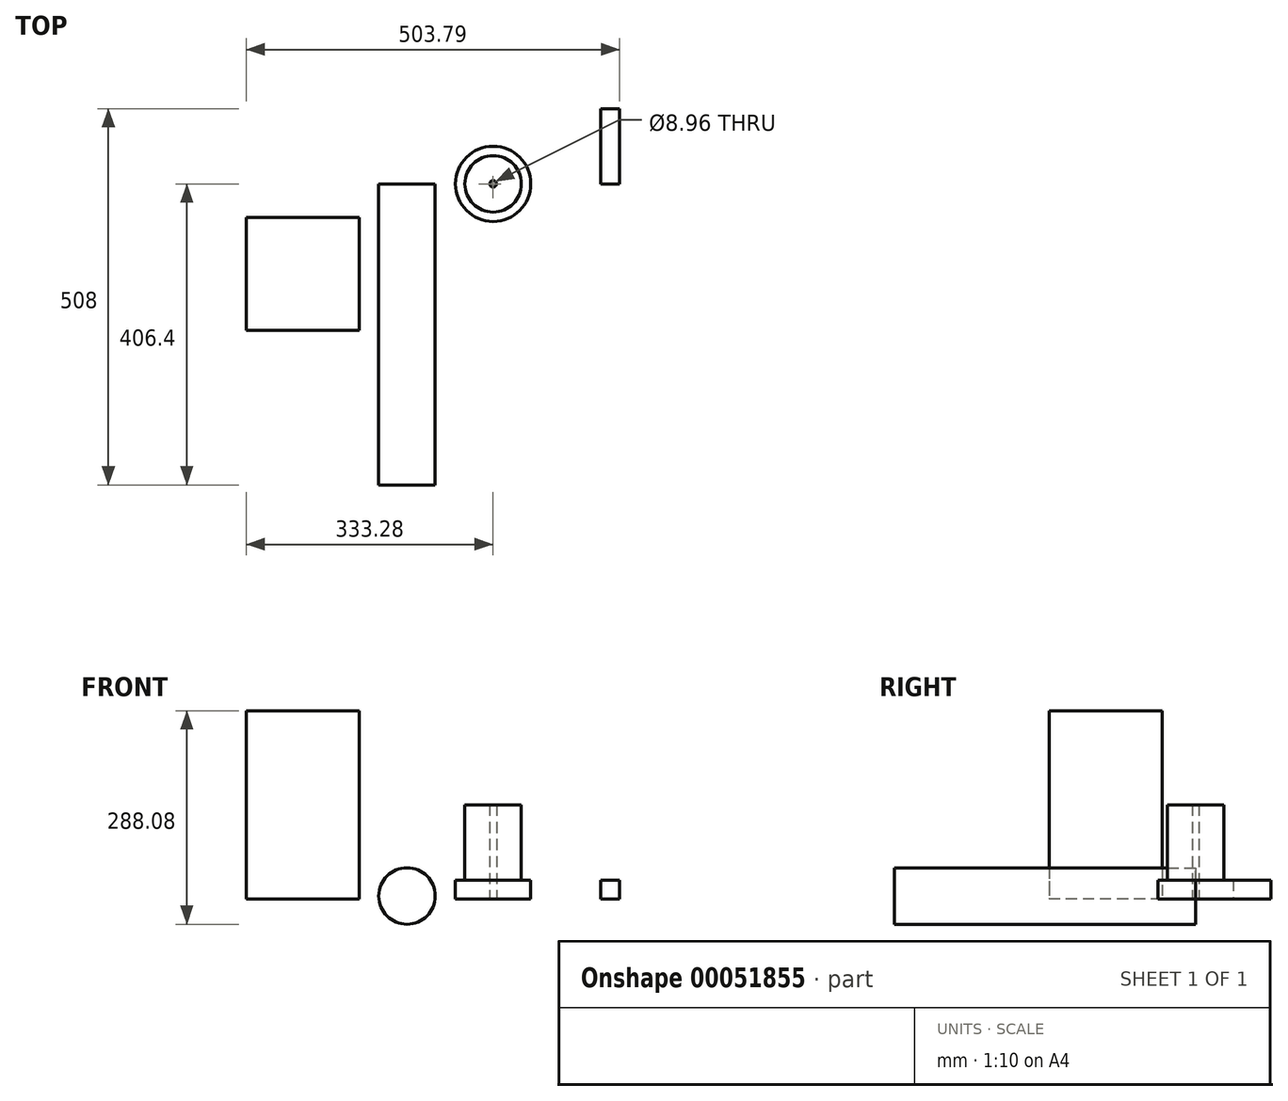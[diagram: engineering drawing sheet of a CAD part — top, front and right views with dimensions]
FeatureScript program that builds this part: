
annotation { "Feature Type Name" : "Feature", "Feature Type Description" : "" }
export const myFeature = defineFeature(function(context is Context, id is Id, definition is map)
    precondition{}
    {
        {
            var Q0;
            Q0=qCreatedBy(makeId("Top.planeOp"),FACE);
            var sketch = newSketch(context, id + "F0", { "sketchPlane" : qUnion([Q0])});
            skCircle(sketch, "E0", {"center": v(0, 0) * mm, "radius": 4.48 * mm});
            skCircle(sketch, "E1", {"center": v(0, 0) * mm, "radius": 50.8 * mm});
            skSolve(sketch);
        }
        {
            var Q0;
            Q0=makeQuery(id+"F0.imprint","IMPRINT",FACE,{"disambiguationData":[TD([[makeQuery(id+"F0.imprint","IMPRINT",EDGE,{"derivedFrom":sQuery(id+"F0.wireOp",EDGE,"E0")}),-1.0]])]});
            extrude(context, id + "F1", {"entities" : qUnion([Q0]), "depth" : 25.4 * mm});
        }
        {
            var Q0;
            Q0=qCreatedBy(makeId("Front.planeOp"),FACE);
            var sketch = newSketch(context, id + "F2", { "sketchPlane" : qUnion([Q0])});
            skCircle(sketch, "E2", {"center": v(-116.2, 4.02) * mm, "radius": 38.1 * mm});
            skSolve(sketch);
        }
        {
            var Q0;
            Q0=makeQuery(id+"F2.imprint","IMPRINT",FACE,{"disambiguationData":[TD([[makeQuery(id+"F2.imprint","IMPRINT",EDGE,{"derivedFrom":sQuery(id+"F2.wireOp",EDGE,"E2")}),1.0]])]});
            extrude(context, id + "F3", {"entities" : qUnion([Q0]), "depth" : 406.4 * mm});
        }
        {
            var Q0;
            Q0=qCreatedBy(makeId("Top.planeOp"),FACE);
            var sketch = newSketch(context, id + "F4", { "sketchPlane" : qUnion([Q0])});
            skLineSegment(sketch, "E3.bottom", {"start": v(-333.28, -45.16) * mm, "end": v(-180.88, -45.16) * mm});
            skLineSegment(sketch, "E3.top", {"start": v(-333.28, -197.56) * mm, "end": v(-180.88, -197.56) * mm});
            skLineSegment(sketch, "E3.left", {"start": v(-333.28, -45.16) * mm, "end": v(-333.28, -197.56) * mm});
            skLineSegment(sketch, "E3.right", {"start": v(-180.88, -45.16) * mm, "end": v(-180.88, -197.56) * mm});
            skSolve(sketch);
        }
        {
            var Q0;
            Q0=makeQuery(id+"F4.imprint","IMPRINT",FACE,{"disambiguationData":[TD([[makeQuery(id+"F4.imprint","IMPRINT",EDGE,{"derivedFrom":sQuery(id+"F4.wireOp",EDGE,"E3.bottom")}),-1.0]])]});
            extrude(context, id + "F5", {"entities" : qUnion([Q0]), "depth" : 254 * mm});
        }
        {
            var Q0;
            Q0=makeQuery(id+"F1.opExtrude","CAP_FACE",FACE,{"disambiguationData":[OSD([sQuery(id+"F0.wireOp",EDGE,"E0"),sQuery(id+"F0.wireOp",EDGE,"E1")])],"isStart":false});
            var sketch = newSketch(context, id + "F6", { "sketchPlane" : qUnion([Q0])});
            skCircle(sketch, "E4", {"center": v(0, 0) * mm, "radius": 38.1 * mm});
            skSolve(sketch);
        }
        {
            var Q0;
            Q0=makeQuery(id+"F6.imprint","IMPRINT",FACE,{"disambiguationData":[TD([[makeQuery(id+"F6.imprint","IMPRINT",EDGE,{"derivedFrom":sQuery(id+"F6.wireOp",EDGE,"E4")}),1.0]])]});
            extrude(context, id + "F7", {"entities" : qUnion([Q0]), "operationType" : NewBodyOperationType.ADD, "depth" : 101.6 * mm});
        }
        {
            var Q0;
            Q0=qCreatedBy(makeId("Top.planeOp"),FACE);
            var sketch = newSketch(context, id + "F8", { "sketchPlane" : qUnion([Q0])});
            skLineSegment(sketch, "E5.bottom", {"start": v(170.5, 0) * mm, "end": v(145.1, 0) * mm});
            skLineSegment(sketch, "E5.top", {"start": v(170.5, 101.6) * mm, "end": v(145.1, 101.6) * mm});
            skLineSegment(sketch, "E5.left", {"start": v(170.5, 0) * mm, "end": v(170.5, 101.6) * mm});
            skLineSegment(sketch, "E5.right", {"start": v(145.1, 0) * mm, "end": v(145.1, 101.6) * mm});
            skSolve(sketch);
        }
        {
            var Q0;
            Q0=makeQuery(id+"F8.imprint","IMPRINT",FACE,{"disambiguationData":[TD([[makeQuery(id+"F8.imprint","IMPRINT",EDGE,{"derivedFrom":sQuery(id+"F8.wireOp",EDGE,"E5.bottom")}),-1.0]])]});
            extrude(context, id + "F9", {"entities" : qUnion([Q0]), "depth" : 25.4 * mm});
        }
    });
